# Revit family: ECH1-835-L24-DW
name_source: partatom
category: Lighting Fixtures
units: mm (PartAtom-declared; Revit-internal decimal feet)

## family parameters
Cut with Voids When Loaded = No
Host = Face
Light Source = Yes
OmniClass Number = 23.80.70.11.14.17
OmniClass Title = Direct/Indirect
Part Type = Normal
Room Calculation Point = No
Round Connector Dimension = Use Diameter
Shared = Yes

## types (1)
- ECH1-835-L24-DW
    Additional Material Finish = Paint - Matte White
    Apparent Load = 164 VA
    Assembly Code = D5020200
    Available Finish Options = Available in Matte White
    Brand = Columbia Lighting
    Color Filter = 16777215
    Color Rendering Index = 80 CRI
    Controller = Please Refer to the Product Spec Sheet for Control Options
    Default Elevation = 48 "
    Description = The ECH is an industry-leading specification high bay providing superior performance and reliability. Available with integral NX Lighting Controls.
    Dimming Lamp Color Temperature Shift = <None>
    Distribution Patterns = None
    Emit Shape Visible in Rendering = No
    Emit from Rectangle Length = 9 "
    Emit from Rectangle Width = 13 "
    Features = Industrial design delivers a small, lightweight fixture for ease of installation
Electrical architecture delivers industry leading efficiencies (up to 201 LPW) that translate into lowest life cycle cost
Designed for unconditioned spaces through a 55 °C ambient temperature rating and a -30°C rating for refrigerated spaces
Wide lumen range (up to 60K) to accommodates various ceiling heights, fixture spacings, and Fc specifications
Optical distribution choices deliver the right light to the right spot (horizontal, vertical, max/min) for your designs
Integrated sensor options for code compliance, increased energy savings, and connection to NX Lighting Controls systems
Optimized bulk packaging minimizes job site space requirements and eases waste removal
    Housing Material = Paint - Matte White
    Installation and Service URL = https://cdn.currentlighting.com
    Lamp = LED
    Lens Material Finish = White Glass
    Load Classification = Lighting
    Manufacturer = Current Lighting
    Model = ECH1-835-L24-DW
    Mounting = Please Refer to the Product Spec Sheet for Mounting Options
    Optical Code = DW
    Photometric Web File = ECH1-835-L24-DW-xxx_120-277V.IES
    Photometric Web Link = https://www.currentlighting.com
    Photometry Note = Please load ies file listed under Photometric Web File for accurate rendering.
    Power Factor = 1
    Product Documentation Link = https://cdn.currentlighting.com
    Product Page URL = https://www.currentlighting.com
    Tilt Angle = -90.00°
    Type Comments = Light Fixture
    URL = www.currentlighting.com
    Version = 2021 V 1.2
    Voltage = 120 V
    Voltage Comments = 120-277;347;480
    Warranty = 5 year limited
    Wattage Comments = 49 - 380 W

## geometry (parser evidence)
native form markers: Sweep x1
no freeform markers — native parametric forms only
